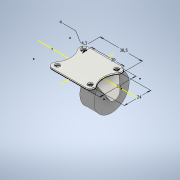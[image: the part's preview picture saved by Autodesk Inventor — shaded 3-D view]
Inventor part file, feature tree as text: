
AUTODESK INVENTOR PART (.ipt)
format: ipt  version: 2021 (Build 250183000, 183)  size: 206,848 bytes
history: native  units: mm
features: extrude x5, sketch x4, revolve x1, mirror x1
ambient origin geometry x8: Origin, YZ Plane, XZ Plane, XY Plane, X Axis, Y Axis, Z Axis, Center Point
bodies: Volumenkörper1 (feature_tree)
feature tree (11):
  extrude  "Extrusion1"  Depth=4.0mm
  sketch  "Skizze2"  dims[d2=24.0mm d3=33.0mm]
  revolve  "Umdrehung1"
  extrude  "Extrusion2"  Depth=33.0mm
  extrude  "Extrusion3"  Depth=38.5mm
  extrude  "Extrusion4"  Depth=3.0mm
  mirror  "Spiegeln1"
  extrude  "Extrusion5"  Depth=1.2mm
  sketch  "Skizze1"  dims[d0=4.0mm d1=30.0mm]
  sketch  "Skizze3"  dims[d4=4.3mm d5=38.5mm]
  sketch  "Skizze4"  dims[d6=1.2mm d7=0.0mm d8=3.0mm d9=32.0mm d10=40.8mm d12=0.0mm d13=10.0mm d14=8.0mm d16=8.0mm d18=24.0mm d20=90.0deg d21=13.0mm d22=0.0mm d23=18.0mm d24=0.0mm d25=1.2mm d26=0.0mm d27=1.2mm d28=1.2mm d29=0.0mm]
